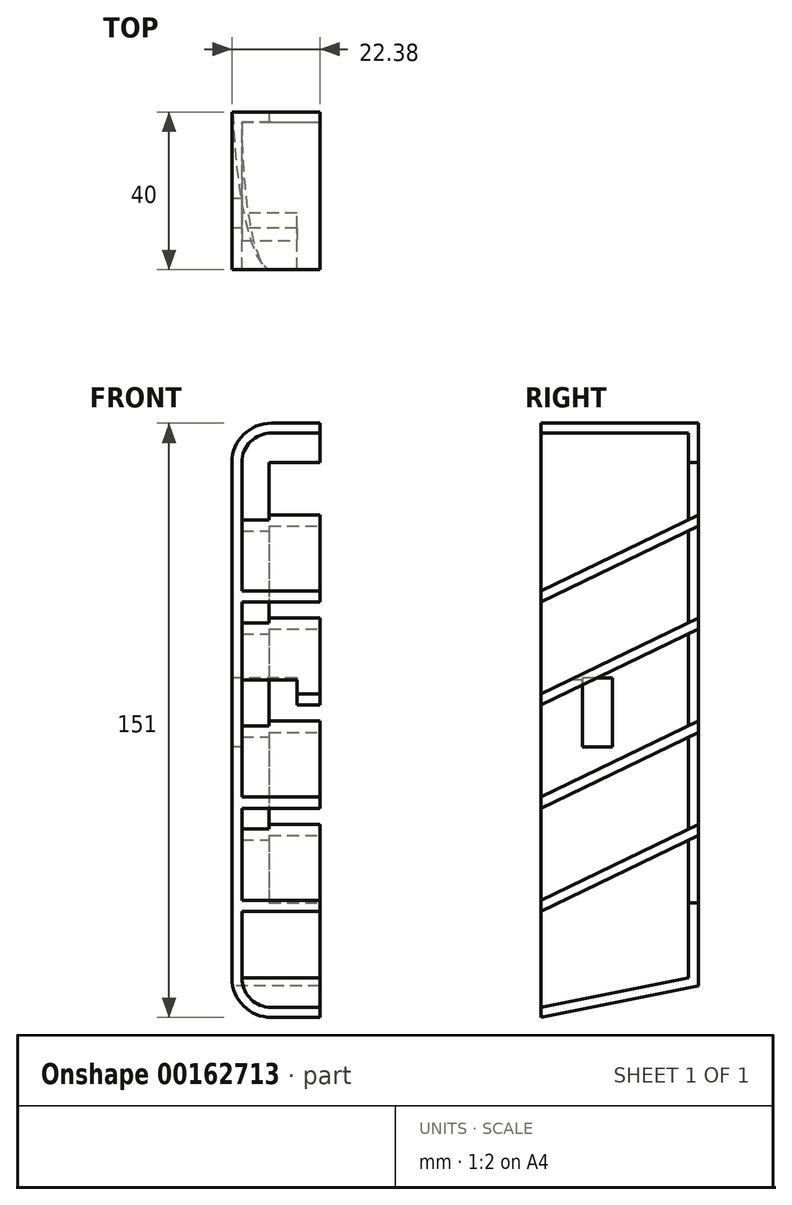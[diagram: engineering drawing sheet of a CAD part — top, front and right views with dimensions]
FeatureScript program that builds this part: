
annotation { "Feature Type Name" : "Feature", "Feature Type Description" : "" }
export const myFeature = defineFeature(function(context is Context, id is Id, definition is map)
    precondition{}
    {
        {
            var Q0;
            Q0=qCreatedBy(makeId("Front.planeOp"),FACE);
            var sketch = newSketch(context, id + "F0", { "sketchPlane" : qUnion([Q0])});
            skLineSegment(sketch, "E0.bottom", {"start": v(-62.5, 75.5) * mm, "end": v(72.5, 75.5) * mm});
            skLineSegment(sketch, "E0.top", {"start": v(-62.5, -75.5) * mm, "end": v(72.5, -75.5) * mm});
            skLineSegment(sketch, "E0.left", {"start": v(-72.5, 65.5) * mm, "end": v(-72.5, -65.5) * mm});
            skLineSegment(sketch, "E0.right", {"start": v(72.5, 75.5) * mm, "end": v(72.5, -75.5) * mm});
            skPoint(sketch, "E0.middle", {"position": v(0, 0) * mm});
            skPoint(sketch, "E1.visualSharp", {"position": v(72.5, 75.5) * mm});
            skPoint(sketch, "E2.visualSharp", {"position": v(72.5, -75.5) * mm});
            skPoint(sketch, "E3.visualSharp", {"position": v(-72.5, 75.5) * mm});
            skArc(sketch, "E3.filletArc", {"start": v(-62.5, 75.5) * mm, "mid": v(-69.57, 72.57) * mm, "end": v(-72.5, 65.5) * mm});
            skPoint(sketch, "E4.visualSharp", {"position": v(-72.5, -75.5) * mm});
            skArc(sketch, "E4.filletArc", {"start": v(-72.5, -65.5) * mm, "mid": v(-69.57, -72.57) * mm, "end": v(-62.5, -75.5) * mm});
            skSolve(sketch);
        }
        {
            var Q0;
            Q0=qSketchRegion(id+"F0",true);
            extrude(context, id + "F1", {"entities" : qUnion([Q0]), "depth" : 40 * mm});
        }
        {
            var Q0;
            Q0=makeQuery(id+"F1.opExtrude","CAP_EDGE",EDGE,{"disambiguationData":[OSD([sQuery(id+"F0.wireOp",EDGE,"E0.top")])],"isStart":true});
            chamfer(context, id + "F2", {"entities" : qUnion([Q0]), "chamferType" : ChamferType.TWO_OFFSETS, "width1" : 40 * mm, "oppositeDirection" : false, "width2" : 8 * mm});
        }
        {
            var Q0;
            Q0=makeQuery(id+"F1.opExtrude","CAP_FACE",FACE,{"disambiguationData":[OSD([sQuery(id+"F0.wireOp",EDGE,"E0.bottom"),sQuery(id+"F0.wireOp",EDGE,"E0.top"),sQuery(id+"F0.wireOp",EDGE,"E0.left"),sQuery(id+"F0.wireOp",EDGE,"E0.right"),sQuery(id+"F0.wireOp",EDGE,"E1.filletArc"),sQuery(id+"F0.wireOp",EDGE,"E2.filletArc")])],"isStart":false});
            shell(context, id + "F3", {"entities" : qUnion([Q0]), "thickness" : 2.54 * mm});
        }
        {
            var Q0;
            Q0=makeQuery(id+"F3.opShell","OFFSET_FACE",FACE,{"disambiguationData":[OSD([sQuery(id+"F0.wireOp",EDGE,"E0.bottom"),sQuery(id+"F0.wireOp",EDGE,"E0.top"),sQuery(id+"F0.wireOp",EDGE,"E0.left"),sQuery(id+"F0.wireOp",EDGE,"E0.right"),sQuery(id+"F0.wireOp",EDGE,"E1.filletArc"),sQuery(id+"F0.wireOp",EDGE,"E2.filletArc")])]});
            var sketch = newSketch(context, id + "F4", { "sketchPlane" : qUnion([Q0])});
            skPoint(sketch, "E5.middle", {"position": v(0, 0) * mm});
            skLineSegment(sketch, "E6.bottom", {"start": v(-63.05, 65.5) * mm, "end": v(62.5, 65.5) * mm});
            skLineSegment(sketch, "E6.top", {"start": v(-63.05, -46.42) * mm, "end": v(62.5, -46.42) * mm});
            skLineSegment(sketch, "E6.left", {"start": v(-63.05, 65.5) * mm, "end": v(-63.05, -46.42) * mm});
            skLineSegment(sketch, "E6.right", {"start": v(62.5, 65.5) * mm, "end": v(62.5, -46.42) * mm});
            skSolve(sketch);
        }
        {
            var Q0;
            Q0=makeQuery(id+"F4.imprint","IMPRINT",FACE,{"disambiguationData":[TD([[makeQuery(id+"F4.imprint","IMPRINT",EDGE,{"derivedFrom":sQuery(id+"F4.wireOp",EDGE,"E6.bottom")}),-1.0]])]});
            extrude(context, id + "F5", {"entities" : qUnion([Q0]), "operationType" : NewBodyOperationType.REMOVE, "oppositeDirection" : true, "depth" : 25.4 * mm});
        }
        {
            var Q0;
            Q0=makeQuery(id+"F3.opShell","OFFSET_FACE",FACE,{"disambiguationData":[OSD([sQuery(id+"F0.wireOp",EDGE,"E0.right")])]});
            var sketch = newSketch(context, id + "F6", { "sketchPlane" : qUnion([Q0])});
            skLineSegment(sketch, "E7.0.0", {"start": v(0, 75.5) * mm, "end": v(0, 75.5) * mm});
            skLineSegment(sketch, "E7.0.1", {"start": v(0, 75.5) * mm, "end": v(40, 75.5) * mm});
            skLineSegment(sketch, "E7.0.2", {"start": v(40, 75.5) * mm, "end": v(40, 75.5) * mm});
            skLineSegment(sketch, "E7.0.3", {"start": v(0, 75.5) * mm, "end": v(40, 75.5) * mm});
            skLineSegment(sketch, "E8.0.0", {"start": v(0, 65.5) * mm, "end": v(0, -67.5) * mm});
            skLineSegment(sketch, "E8.0.1", {"start": v(0, -67.5) * mm, "end": v(40, -75.5) * mm});
            skLineSegment(sketch, "E8.0.2", {"start": v(40, -75.5) * mm, "end": v(40, 65.5) * mm});
            skLineSegment(sketch, "E8.0.3", {"start": v(40, 65.5) * mm, "end": v(0, 65.5) * mm});
            skCircle(sketch, "E9", {"center": v(21.36, 0) * mm, "radius": 3.18 * mm});
            skCircle(sketch, "E10.0.1.0", {"center": v(21.36, -30) * mm, "radius": 3.18 * mm});
            skLineSegment(sketch, "E10.direction2", {"start": v(21.36, 0) * mm, "end": v(21.36, -30) * mm, "construction": true});
            skCircle(sketch, "E11", {"center": v(21.36, 35) * mm, "radius": 3.18 * mm});
            skSolve(sketch);
        }
        {
            var Q0;
            Q0=makeQuery(id+"F6.imprint","IMPRINT",FACE,{"disambiguationData":[TD([[makeQuery(id+"F6.imprint","IMPRINT",EDGE,{"derivedFrom":sQuery(id+"F6.wireOp",EDGE,"E9")}),1.0]])]});
            var Q1;
            Q1=makeQuery(id+"F6.imprint","IMPRINT",FACE,{"disambiguationData":[TD([[makeQuery(id+"F6.imprint","IMPRINT",EDGE,{"derivedFrom":sQuery(id+"F6.wireOp",EDGE,"E11")}),1.0]])]});
            var Q2;
            Q2=makeQuery(id+"F6.imprint","IMPRINT",FACE,{"disambiguationData":[TD([[makeQuery(id+"F6.imprint","IMPRINT",EDGE,{"derivedFrom":sQuery(id+"F6.wireOp",EDGE,"E10.0.1.0")}),1.0]])]});
            var Q3;
            Q3=sQuery(id+"F6.wireOp",EDGE,"E11");
            var Q4;
            Q4=sQuery(id+"F6.wireOp",EDGE,"E9");
            var Q5;
            Q5=sQuery(id+"F6.wireOp",EDGE,"E10.0.1.0");
            extrude(context, id + "F7", {"entities" : qUnion([Q0, Q1, Q2]), "operationType" : NewBodyOperationType.REMOVE, "surfaceEntities" : qUnion([Q3, Q4, Q5]), "oppositeDirection" : true, "depth" : 19.05 * mm});
        }
        {
            var Q0;
            Q0=makeQuery(id+"F3.opShell","OFFSET_FACE",FACE,{"disambiguationData":[OSD([sQuery(id+"F0.wireOp",EDGE,"E0.right")])]});
            var sketch = newSketch(context, id + "F8", { "sketchPlane" : qUnion([Q0])});
            skLineSegment(sketch, "E12", {"start": v(40, -48.55) * mm, "end": v(0, -29.24) * mm});
            skLineSegment(sketch, "E13", {"start": v(0, -29.24) * mm, "end": v(0, -26.41) * mm});
            skLineSegment(sketch, "E14", {"start": v(0, -26.41) * mm, "end": v(40, -45.73) * mm});
            skLineSegment(sketch, "E15", {"start": v(40, -45.73) * mm, "end": v(40, -48.55) * mm});
            skLineSegment(sketch, "E16", {"start": v(40, -22.36) * mm, "end": v(0, -3.05) * mm});
            skLineSegment(sketch, "E17", {"start": v(0, -3.05) * mm, "end": v(0, -0.23) * mm});
            skLineSegment(sketch, "E18", {"start": v(0, -0.23) * mm, "end": v(40, -19.54) * mm});
            skLineSegment(sketch, "E19", {"start": v(40, -19.54) * mm, "end": v(40, -22.36) * mm});
            skLineSegment(sketch, "E20", {"start": v(40, 3.83) * mm, "end": v(0, 23.14) * mm});
            skLineSegment(sketch, "E21", {"start": v(0, 23.14) * mm, "end": v(0, 25.96) * mm});
            skLineSegment(sketch, "E22", {"start": v(0, 25.96) * mm, "end": v(40, 6.65) * mm});
            skLineSegment(sketch, "E23", {"start": v(40, 6.65) * mm, "end": v(40, 3.83) * mm});
            skLineSegment(sketch, "E24", {"start": v(40, 30.01) * mm, "end": v(0, 49.33) * mm});
            skLineSegment(sketch, "E25", {"start": v(0, 49.33) * mm, "end": v(0, 52.15) * mm});
            skLineSegment(sketch, "E26", {"start": v(0, 52.15) * mm, "end": v(40, 32.84) * mm});
            skLineSegment(sketch, "E27", {"start": v(40, 32.84) * mm, "end": v(40, 30.01) * mm});
            skSolve(sketch);
        }
        {
            var Q0;
            Q0=qSketchRegion(id+"F8",true);
            extrude(context, id + "F9", {"entities" : qUnion([Q0]), "operationType" : NewBodyOperationType.ADD, "depth" : 142.24 * mm});
        }
        {
            var Q0;
            Q0=makeQuery(id+"F1.opExtrude","SWEPT_FACE",FACE,{"disambiguationData":[OSD([sQuery(id+"F0.wireOp",EDGE,"E0.left")])]});
            var sketch = newSketch(context, id + "F10", { "sketchPlane" : qUnion([Q0])});
            skLineSegment(sketch, "E28.bottom", {"start": v(21.9, 10.75) * mm, "end": v(29.4, 10.75) * mm});
            skLineSegment(sketch, "E28.top", {"start": v(21.9, -6.75) * mm, "end": v(29.4, -6.75) * mm});
            skLineSegment(sketch, "E28.left", {"start": v(21.9, 10.75) * mm, "end": v(21.9, -6.75) * mm});
            skLineSegment(sketch, "E28.right", {"start": v(29.4, 10.75) * mm, "end": v(29.4, -6.75) * mm});
            skSolve(sketch);
        }
        {
            var Q0;
            Q0=makeQuery(id+"F10.imprint","IMPRINT",FACE,{"disambiguationData":[TD([[makeQuery(id+"F10.imprint","IMPRINT",EDGE,{"derivedFrom":sQuery(id+"F10.wireOp",EDGE,"E28.bottom")}),-1.0]])]});
            var Q1;
            Q1=qSketchRegion(id+"FNYe9KNpvqW2HJJ_1",true);
            extrude(context, id + "F11", {"entities" : qUnion([Q0, Q1]), "operationType" : NewBodyOperationType.REMOVE, "oppositeDirection" : true, "depth" : 16.5 * mm});
        }
        {
            var Q0;
            {var subQ3=sQuery(id+"F0.wireOp",EDGE,"E0.left");Q0=makeQuery(id+"F9.boolean.opBoolean","SPLIT",FACE,{"disambiguationData":[TD([makeQuery(id+"F9.opExtrude","SWEPT_FACE",FACE,{"disambiguationData":[OSD([sQuery(id+"F8.wireOp",EDGE,"E18")])]})])],"derivedFrom":makeQuery(id+"F3.opShell","OFFSET_FACE",FACE,{"disambiguationData":[OSD([subQ3])]})});}
            var sketch = newSketch(context, id + "F12", { "sketchPlane" : qUnion([Q0])});
            skLineSegment(sketch, "E29.bottom", {"start": v(-29.4, -6.75) * mm, "end": v(-46.16, -6.75) * mm});
            skLineSegment(sketch, "E29.top", {"start": v(-29.4, 10.22) * mm, "end": v(-46.16, 10.22) * mm});
            skLineSegment(sketch, "E29.left", {"start": v(-29.4, -6.75) * mm, "end": v(-29.4, 10.22) * mm});
            skLineSegment(sketch, "E29.right", {"start": v(-46.16, -6.75) * mm, "end": v(-46.16, 10.22) * mm});
            skSolve(sketch);
        }
        {
            var Q0;
            {var subQ11=sQuery(id+"F12.wireOp",EDGE,"E29.top");Q0=makeQuery(id+"F12.imprint","IMPRINT",FACE,{"disambiguationData":[TD([[makeQuery(id+"F12.imprint","IMPRINT",EDGE,{"derivedFrom":subQ11}),1.0]])]});}
            extrude(context, id + "F13", {"entities" : qUnion([Q0]), "operationType" : NewBodyOperationType.REMOVE, "depth" : 14 * mm});
        }
        {
            var Q0;
            Q0=makeQuery(id+"F9.boolean.opBoolean","MERGE",FACE,{"derivedFrom":[makeQuery(id+"F1.opExtrude","CAP_FACE",FACE,{"disambiguationData":[OSD([sQuery(id+"F0.wireOp",EDGE,"E0.bottom"),sQuery(id+"F0.wireOp",EDGE,"E0.top"),sQuery(id+"F0.wireOp",EDGE,"E0.left"),sQuery(id+"F0.wireOp",EDGE,"E0.right"),sQuery(id+"F0.wireOp",EDGE,"E3.filletArc"),sQuery(id+"F0.wireOp",EDGE,"E4.filletArc")])],"isStart":false}),makeQuery(id+"F9.opExtrude","SWEPT_FACE",FACE,{"disambiguationData":[OSD([sQuery(id+"F8.wireOp",EDGE,"E15")])]}),makeQuery(id+"F9.opExtrude","SWEPT_FACE",FACE,{"disambiguationData":[OSD([sQuery(id+"F8.wireOp",EDGE,"E19")])]}),makeQuery(id+"F9.opExtrude","SWEPT_FACE",FACE,{"disambiguationData":[OSD([sQuery(id+"F8.wireOp",EDGE,"E23")])]}),makeQuery(id+"F9.opExtrude","SWEPT_FACE",FACE,{"disambiguationData":[OSD([sQuery(id+"F8.wireOp",EDGE,"E27")])]})]});
            var sketch = newSketch(context, id + "F14", { "sketchPlane" : qUnion([Q0])});
            skLineSegment(sketch, "E30.bottom", {"start": v(77.08, 77.18) * mm, "end": v(-50.12, 77.18) * mm});
            skLineSegment(sketch, "E30.top", {"start": v(77.08, -86.17) * mm, "end": v(-50.12, -86.17) * mm});
            skLineSegment(sketch, "E30.left", {"start": v(77.08, 77.18) * mm, "end": v(77.08, -86.17) * mm});
            skLineSegment(sketch, "E30.right", {"start": v(-50.12, 77.18) * mm, "end": v(-50.12, -86.17) * mm});
            skSolve(sketch);
        }
        {
            var Q0;
            Q0 = qSketchRegion(id + "F14", true);
            extrude(context, id + "F15", {"entities" : qUnion([Q0]), "operationType" : NewBodyOperationType.REMOVE, "oppositeDirection" : true, "depth" : 125 * mm, "symmetric" : true});
        }
    });
